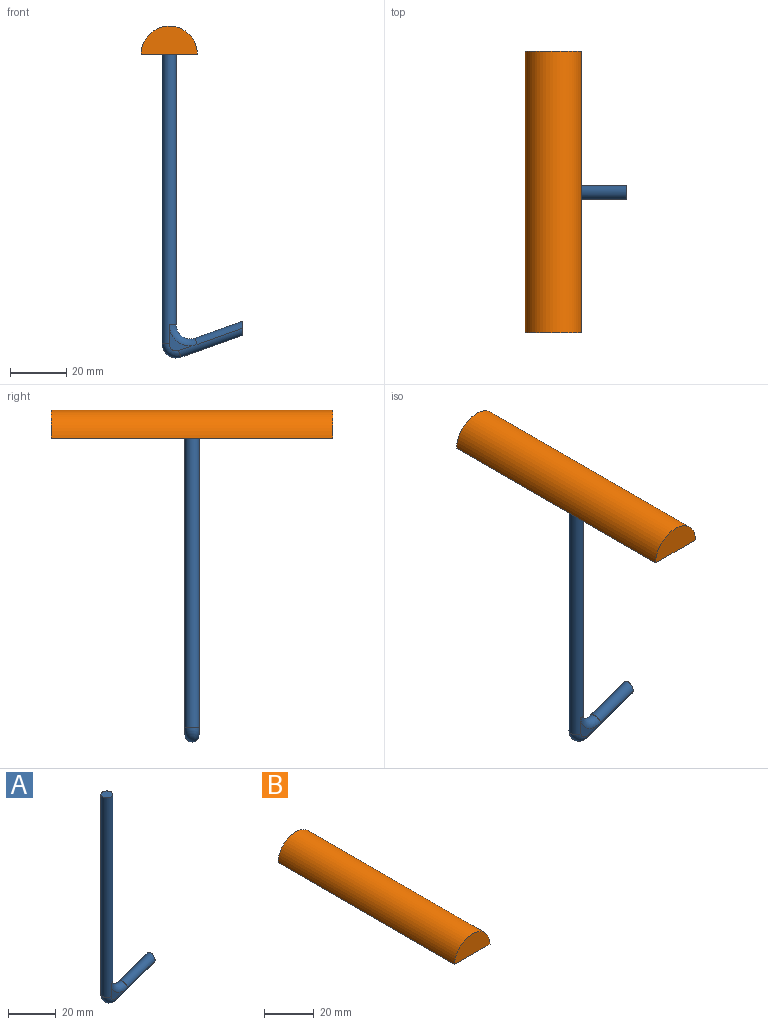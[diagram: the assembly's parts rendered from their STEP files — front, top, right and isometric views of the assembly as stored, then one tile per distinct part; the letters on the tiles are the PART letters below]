
ASSEMBLY  parts=2 mates=1
PART A: 9 faces, bbox 29.9x5x108.3 mm
  f0: plane 5x5mm, normal (0,0,1), area 19.6mm2, adj f6
  f1: plane 5x4.99mm, normal (1,0,0), area 19.3mm2, adj f4,f7
  f2: plane 9.27x7.97mm, normal (0,-1,0), area 20.3mm2, adj f4,f5,f6,f8
  f3: plane 9.27x7.97mm, normal (0,1,0), area 20.3mm2, adj f4,f5,f6,f8
  f4: cylinder r=2.5mm len=23.64mm, axis (-0.94,0,-0.33), area 180.6mm2, adj f1,f2,f3,f5,f7,f8
  f5: torus R=2.5mm, axis (0,-1,0), area 61.4mm2, adj f2,f3,f4,f6
  f6: cylinder r=2.5mm len=102.93mm, axis (0,0,1), area 1563.6mm2, adj f0,f2,f3,f5,f8
  f7: cylinder r=2.5mm len=17.81mm, axis (0.94,0,0.33), area 134.4mm2, adj f1,f4,f8
  f8: torus R=7.5mm, axis (0,-1,0), area 88.3mm2, adj f2,f3,f4,f6,f7
PART B: 6 faces, bbox 20x100x10 mm
  f0: cylinder r=10mm len=100mm, axis (0,1,0), area 3141.6mm2, adj f1,f2,f3
  f1: plane 100x20mm, normal (0,0,-1), area 1980.4mm2, adj f0,f2,f3,f4
  f2: plane 20x10mm, normal (0,-1,0), area 157.1mm2, adj f0,f1
  f3: plane 20x10mm, normal (0,1,0), area 157.1mm2, adj f0,f1
  f4: cylinder r=2.5mm len=5mm, axis (0,0,-1), area 47.1mm2, adj f1,f5
  f5: plane 5x5mm, normal (0,0,-1), area 19.6mm2, adj f4
PLACE A t=(-2.75,2.29,-49)mm
PLACE B t=(-0.85,49.79,-5.1)mm
MATE fastened A.f6 <-> B.f1  axis (0,0,1) through (-0.25,-0.21,-5.1)mm
